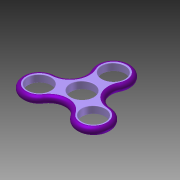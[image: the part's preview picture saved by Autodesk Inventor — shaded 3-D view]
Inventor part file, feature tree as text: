
AUTODESK INVENTOR PART (.ipt)
format: ipt  version: 2011 SP2 (Build 150309200, 309)  size: 185,856 bytes
history: native  units: mm
features: fillet x2, extrude x1, sketch x1
ambient origin geometry x8: Origin, YZ Plane, XZ Plane, XY Plane, X Axis, Y Axis, Z Axis, Center Point
bodies: Solid1 (feature_tree)
feature tree (4):
  extrude  "Extrusion1"  Depth=22.0mm
  fillet  "Fillet1"  Radius=30.0mm
  fillet  "Fillet2"  Radius=5.0mm
  sketch  "Sketch1"  dims[d0=11.0mm d1=22.0mm d2=30.0mm d3=5.0mm d4=30.0mm d6=360.0deg d8=15.0mm d9=15.0mm d10=15.0mm d11=7.0mm d12=0.0mm d13=0.5mm]
